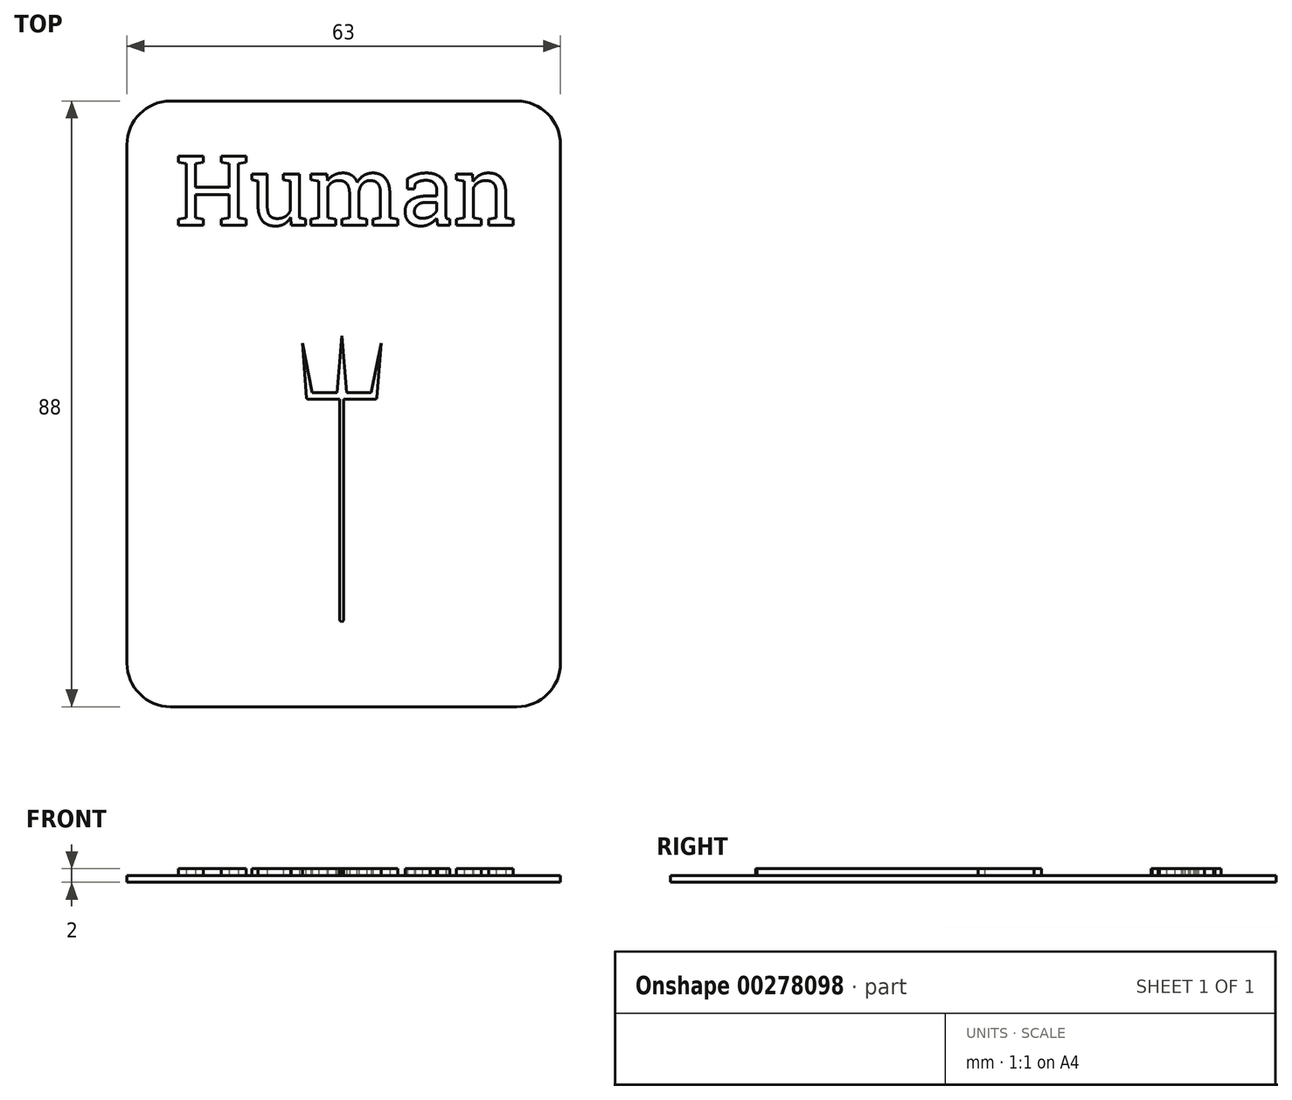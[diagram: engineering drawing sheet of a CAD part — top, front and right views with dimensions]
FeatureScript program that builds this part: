
annotation { "Feature Type Name" : "Feature", "Feature Type Description" : "" }
export const myFeature = defineFeature(function(context is Context, id is Id, definition is map)
    precondition{}
    {
        {
            var Q0;
            Q0=qCreatedBy(makeId("Top.planeOp"),FACE);
            var sketch = newSketch(context, id + "F0", { "sketchPlane" : qUnion([Q0])});
            skLineSegment(sketch, "E0.bottom", {"start": v(-29.69, 39.64) * mm, "end": v(20.61, 39.64) * mm});
            skLineSegment(sketch, "E0.top", {"start": v(-29.69, -48.36) * mm, "end": v(20.61, -48.36) * mm});
            skLineSegment(sketch, "E0.left", {"start": v(-36.04, 33.3) * mm, "end": v(-36.04, -42) * mm});
            skLineSegment(sketch, "E0.right", {"start": v(26.96, 33.3) * mm, "end": v(26.96, -42) * mm});
            skPoint(sketch, "E1.visualSharp", {"position": v(-36.04, 39.64) * mm});
            skArc(sketch, "E1.filletArc", {"start": v(-29.69, 39.64) * mm, "mid": v(-34.18, 37.78) * mm, "end": v(-36.04, 33.3) * mm});
            skPoint(sketch, "E2.visualSharp", {"position": v(26.96, 39.64) * mm});
            skArc(sketch, "E2.filletArc", {"start": v(26.96, 33.3) * mm, "mid": v(25.1, 37.78) * mm, "end": v(20.61, 39.64) * mm});
            skPoint(sketch, "E3.visualSharp", {"position": v(26.96, -48.36) * mm});
            skArc(sketch, "E3.filletArc", {"start": v(20.61, -48.36) * mm, "mid": v(25.1, -46.5) * mm, "end": v(26.96, -42) * mm});
            skPoint(sketch, "E4.visualSharp", {"position": v(-36.04, -48.36) * mm});
            skArc(sketch, "E4.filletArc", {"start": v(-36.04, -42) * mm, "mid": v(-34.18, -46.5) * mm, "end": v(-29.69, -48.36) * mm});
            skSolve(sketch);
        }
        {
            var Q0;
            Q0=makeQuery(id+"F0.imprint","IMPRINT",FACE,{"disambiguationData":[TD([[makeQuery(id+"F0.imprint","IMPRINT",EDGE,{"derivedFrom":sQuery(id+"F0.wireOp",EDGE,"E0.bottom")}),-1.0]])]});
            extrude(context, id + "F1", {"entities" : qUnion([Q0]), "depth" : 1 * mm});
        }
        {
            var Q0;
            Q0=makeQuery(id+"F1.opExtrude","CAP_FACE",FACE,{"disambiguationData":[OSD([sQuery(id+"F0.wireOp",EDGE,"E0.bottom"),sQuery(id+"F0.wireOp",EDGE,"E0.top"),sQuery(id+"F0.wireOp",EDGE,"E0.left"),sQuery(id+"F0.wireOp",EDGE,"E0.right"),sQuery(id+"F0.wireOp",EDGE,"E1.filletArc"),sQuery(id+"F0.wireOp",EDGE,"E2.filletArc"),sQuery(id+"F0.wireOp",EDGE,"E3.filletArc"),sQuery(id+"F0.wireOp",EDGE,"E4.filletArc")])],"isStart":false});
            var sketch = newSketch(context, id + "F2", { "sketchPlane" : qUnion([Q0])});
            skLineSegment(sketch, "E5", {"start": v(-4.84, 5.52) * mm, "end": v(-5.53, -2.72) * mm});
            skLineSegment(sketch, "E6.MirrorCS", {"start": v(-4.84, 5.52) * mm, "end": v(-4.14, -2.72) * mm});
            skLineSegment(sketch, "E7", {"start": v(-9.94, -3.45) * mm, "end": v(-10.55, 4.47) * mm});
            skLineSegment(sketch, "E8", {"start": v(-5.53, -2.72) * mm, "end": v(-9.14, -2.72) * mm});
            skLineSegment(sketch, "E9", {"start": v(-9.14, -2.72) * mm, "end": v(-10.55, 4.47) * mm});
            skLineSegment(sketch, "E10.MirrorCS", {"start": v(-4.14, -2.72) * mm, "end": v(-0.54, -2.72) * mm});
            skLineSegment(sketch, "E11.MirrorCS", {"start": v(-0.54, -2.72) * mm, "end": v(0.87, 4.47) * mm});
            skLineSegment(sketch, "E12.MirrorCS", {"start": v(0.27, -3.45) * mm, "end": v(0.87, 4.47) * mm});
            skPoint(sketch, "E13.visualSharp", {"position": v(-9.92, -3.68) * mm});
            skArc(sketch, "E13.filletArc", {"start": v(-9.94, -3.45) * mm, "mid": v(-9.86, -3.61) * mm, "end": v(-9.7, -3.68) * mm});
            skPoint(sketch, "E14.visualSharp", {"position": v(0.25, -3.68) * mm});
            skArc(sketch, "E14.filletArc", {"start": v(0.02, -3.68) * mm, "mid": v(0.2, -3.61) * mm, "end": v(0.27, -3.45) * mm});
            skLineSegment(sketch, "E15", {"start": v(-5.12, -3.68) * mm, "end": v(-5.12, -35.8) * mm});
            skLineSegment(sketch, "E16", {"start": v(-5.12, -35.8) * mm, "end": v(-4.84, -36.03) * mm});
            skLineSegment(sketch, "E17.MirrorCS", {"start": v(-4.56, -3.68) * mm, "end": v(-4.56, -35.8) * mm});
            skLineSegment(sketch, "E18.MirrorCS", {"start": v(-4.56, -35.8) * mm, "end": v(-4.84, -36.03) * mm});
            skLineSegment(sketch, "E19", {"start": v(-5.12, -3.68) * mm, "end": v(-9.7, -3.68) * mm});
            skLineSegment(sketch, "E20", {"start": v(0.02, -3.68) * mm, "end": v(-4.56, -3.68) * mm});
            skSolve(sketch);
        }
        {
            var Q0;
            Q0 = qSketchRegion(id + "F2", true);
            extrude(context, id + "F3", {"entities" : qUnion([Q0]), "operationType" : NewBodyOperationType.ADD, "depth" : 1 * mm});
        }
        {
            var Q0;
            Q0=makeQuery(id+"F2.imprint","IMPRINT",FACE,{"disambiguationData":[TD([[makeQuery(id+"F2.imprint","IMPRINT",EDGE,{"derivedFrom":sQuery(id+"F2.wireOp",EDGE,"E5")}),1.0]])]});
            var sketch = newSketch(context, id + "F4", { "sketchPlane" : qUnion([Q0])});
            skText(sketch, "E21", { "text": "Human", "fontName": "RobotoSlab-Regular.ttf"});
            const initialGuessF4  = {"E21": [-0.02902, 0.02162, 1, 0, 0.01014]};
            skSetInitialGuess(sketch, initialGuessF4);
            skSolve(sketch);
        }
        {
            var Q0;
            Q0 = qSketchRegion(id + "F4", true);
            extrude(context, id + "F5", {"entities" : qUnion([Q0]), "operationType" : NewBodyOperationType.ADD, "depth" : 1 * mm});
        }
    });
